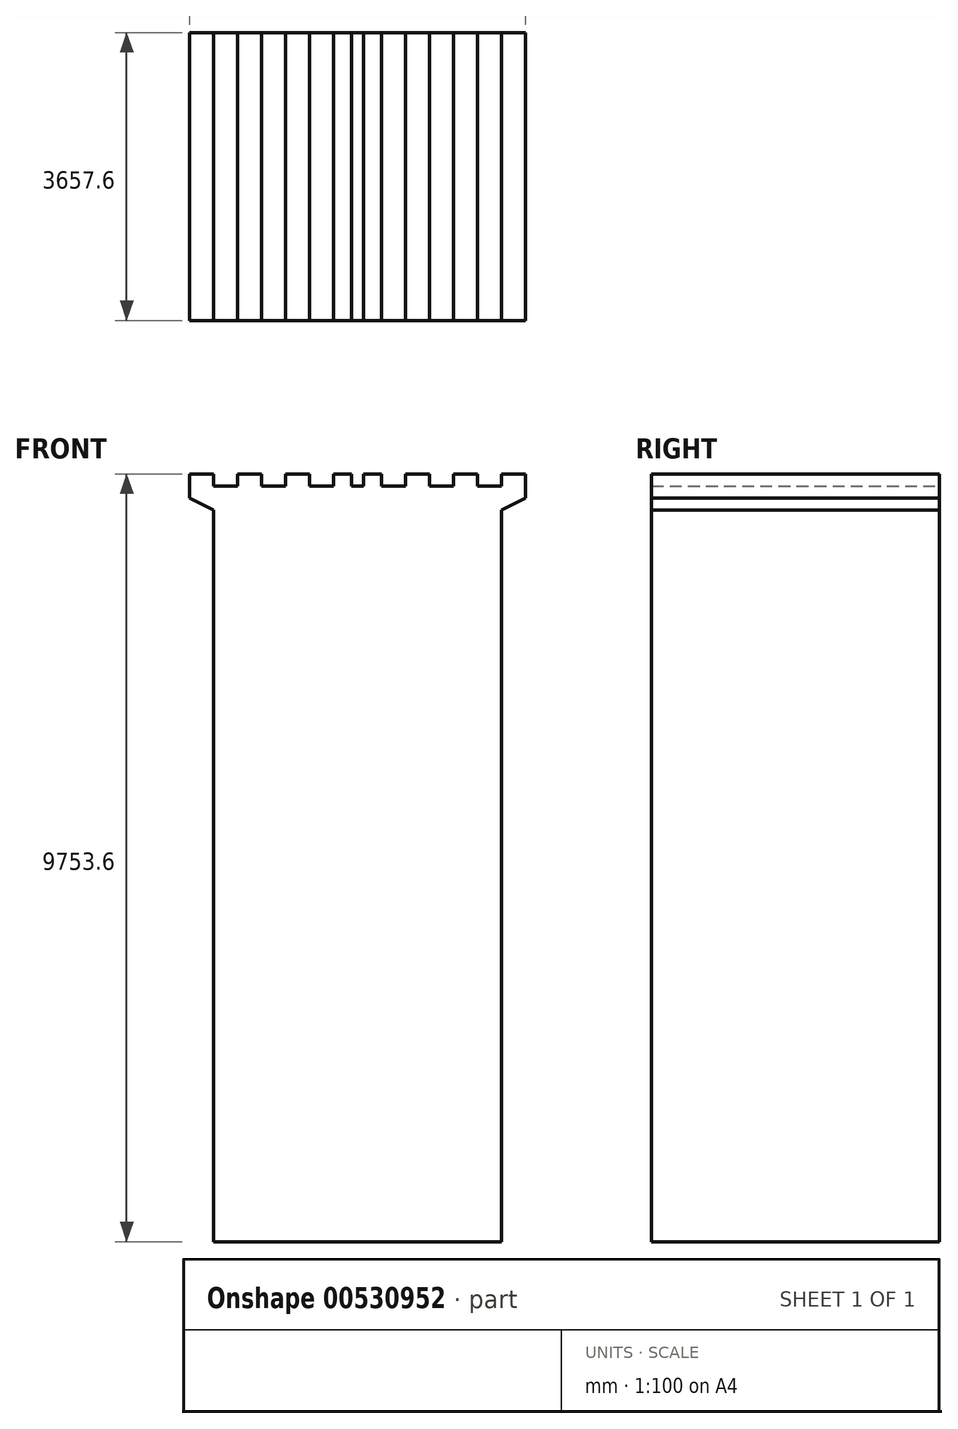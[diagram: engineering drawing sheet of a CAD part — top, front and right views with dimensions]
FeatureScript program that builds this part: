
annotation { "Feature Type Name" : "Feature", "Feature Type Description" : "" }
export const myFeature = defineFeature(function(context is Context, id is Id, definition is map)
    precondition{}
    {
        {
            var Q0;
            Q0=qCreatedBy(makeId("Front.planeOp"),FACE);
            var sketch = newSketch(context, id + "F0", { "sketchPlane" : qUnion([Q0])});
            skLineSegment(sketch, "E0.top", {"start": v(-3041.28, -5600.17) * mm, "end": v(616.32, -5600.17) * mm});
            skLineSegment(sketch, "E0.left", {"start": v(-3041.28, 3696.23) * mm, "end": v(-3041.28, -5600.17) * mm});
            skLineSegment(sketch, "E0.right", {"start": v(616.32, 3696.23) * mm, "end": v(616.32, -5600.17) * mm});
            skPoint(sketch, "E1.firstSnap0", {"position": v(-1212.48, 3848.63) * mm});
            skLineSegment(sketch, "E1.top", {"start": v(921.12, 4153.43) * mm, "end": v(616.32, 4153.43) * mm});
            skLineSegment(sketch, "E1.left", {"start": v(921.12, 3848.63) * mm, "end": v(921.12, 4153.43) * mm});
            skLineSegment(sketch, "E1.right", {"start": v(-3346.08, 3848.63) * mm, "end": v(-3346.08, 4153.43) * mm});
            skLineSegment(sketch, "E2", {"start": v(-3041.28, 4153.43) * mm, "end": v(-3041.28, 4001.03) * mm});
            skLineSegment(sketch, "E3", {"start": v(-3041.28, 4001.03) * mm, "end": v(-2736.48, 4001.03) * mm});
            skLineSegment(sketch, "E4", {"start": v(-2736.48, 4001.03) * mm, "end": v(-2736.48, 4153.43) * mm});
            skLineSegment(sketch, "E5.trimOffspring", {"start": v(-3041.28, 4153.43) * mm, "end": v(-3346.08, 4153.43) * mm});
            skLineSegment(sketch, "E6", {"start": v(-3346.08, 3848.63) * mm, "end": v(-3041.28, 3696.23) * mm});
            skPoint(sketch, "E7.orphan", {"position": v(-3041.28, 3848.63) * mm});
            skLineSegment(sketch, "E8.MirrorCS", {"start": v(-2431.68, 4153.43) * mm, "end": v(-2431.68, 4001.03) * mm});
            skLineSegment(sketch, "E9", {"start": v(-2431.68, 4001.03) * mm, "end": v(-2126.88, 4001.03) * mm});
            skLineSegment(sketch, "E10", {"start": v(-2126.88, 4001.03) * mm, "end": v(-2126.88, 4153.43) * mm});
            skLineSegment(sketch, "E11.trimOffspring", {"start": v(-2431.68, 4153.43) * mm, "end": v(-2736.48, 4153.43) * mm});
            skLineSegment(sketch, "E12", {"start": v(-2584.08, 4153.43) * mm, "end": v(-2584.08, 4001.03) * mm, "construction": true});
            skLineSegment(sketch, "E13", {"start": v(-2279.28, 4001.03) * mm, "end": v(-2279.28, 4153.43) * mm, "construction": true});
            skLineSegment(sketch, "E14.MirrorCS", {"start": v(-2888.88, 4001.03) * mm, "end": v(-2888.88, 4153.43) * mm, "construction": true});
            skLineSegment(sketch, "E15", {"start": v(-2126.88, 4001.03) * mm, "end": v(-1974.48, 4001.03) * mm, "construction": true});
            skLineSegment(sketch, "E16", {"start": v(-1974.48, 4001.03) * mm, "end": v(-1822.08, 4001.03) * mm, "construction": true});
            skLineSegment(sketch, "E17", {"start": v(-1822.08, 4001.03) * mm, "end": v(-1669.68, 4001.03) * mm, "construction": true});
            skLineSegment(sketch, "E18", {"start": v(-1669.68, 4001.03) * mm, "end": v(-1517.28, 4001.03) * mm, "construction": true});
            skLineSegment(sketch, "E19", {"start": v(-1517.28, 4001.03) * mm, "end": v(-1364.88, 4001.03) * mm, "construction": true});
            skLineSegment(sketch, "E20", {"start": v(-1364.88, 4001.03) * mm, "end": v(-1212.48, 4001.03) * mm, "construction": true});
            skLineSegment(sketch, "E21", {"start": v(-1212.48, 4001.03) * mm, "end": v(-1060.08, 4001.03) * mm, "construction": true});
            skLineSegment(sketch, "E22", {"start": v(-1822.08, 4001.03) * mm, "end": v(-1822.08, 4153.43) * mm});
            skLineSegment(sketch, "E23", {"start": v(-1822.08, 4001.03) * mm, "end": v(-1517.28, 4001.03) * mm});
            skLineSegment(sketch, "E24", {"start": v(-1517.28, 4001.03) * mm, "end": v(-1517.28, 4153.43) * mm});
            skLineSegment(sketch, "E25.trimOffspring", {"start": v(-1822.08, 4153.43) * mm, "end": v(-2126.88, 4153.43) * mm});
            skLineSegment(sketch, "E26", {"start": v(-1212.48, 3848.63) * mm, "end": v(-1212.48, -5600.17) * mm, "construction": true});
            skLineSegment(sketch, "E27.MirrorCS", {"start": v(-602.88, 4001.03) * mm, "end": v(-907.68, 4001.03) * mm});
            skLineSegment(sketch, "E28.MirrorCS", {"start": v(-602.88, 4001.03) * mm, "end": v(-755.28, 4001.03) * mm, "construction": true});
            skLineSegment(sketch, "E29.MirrorCS", {"start": v(-602.88, 4001.03) * mm, "end": v(-602.88, 4153.43) * mm});
            skLineSegment(sketch, "E30.MirrorCS", {"start": v(-450.48, 4001.03) * mm, "end": v(-602.88, 4001.03) * mm, "construction": true});
            skLineSegment(sketch, "E31.MirrorCS", {"start": v(-907.68, 4001.03) * mm, "end": v(-907.68, 4153.43) * mm});
            skLineSegment(sketch, "E32.MirrorCS", {"start": v(-755.28, 4001.03) * mm, "end": v(-907.68, 4001.03) * mm, "construction": true});
            skLineSegment(sketch, "E33.MirrorCS", {"start": v(6.72, 4153.43) * mm, "end": v(311.52, 4153.43) * mm});
            skLineSegment(sketch, "E34.MirrorCS", {"start": v(311.52, 4001.03) * mm, "end": v(311.52, 4153.43) * mm});
            skLineSegment(sketch, "E35.MirrorCS", {"start": v(6.72, 4153.43) * mm, "end": v(6.72, 4001.03) * mm});
            skLineSegment(sketch, "E36.MirrorCS", {"start": v(-907.68, 4001.03) * mm, "end": v(-1060.08, 4001.03) * mm, "construction": true});
            skLineSegment(sketch, "E37.MirrorCS", {"start": v(463.92, 4001.03) * mm, "end": v(463.92, 4153.43) * mm, "construction": true});
            skLineSegment(sketch, "E38.MirrorCS", {"start": v(-145.68, 4001.03) * mm, "end": v(-145.68, 4153.43) * mm, "construction": true});
            skLineSegment(sketch, "E39.MirrorCS", {"start": v(616.32, 4153.43) * mm, "end": v(616.32, 4001.03) * mm});
            skLineSegment(sketch, "E40.MirrorCS", {"start": v(-298.08, 4001.03) * mm, "end": v(-298.08, 4153.43) * mm});
            skLineSegment(sketch, "E41.MirrorCS", {"start": v(6.72, 4001.03) * mm, "end": v(-298.08, 4001.03) * mm});
            skLineSegment(sketch, "E42.MirrorCS", {"start": v(-298.08, 4001.03) * mm, "end": v(-450.48, 4001.03) * mm, "construction": true});
            skLineSegment(sketch, "E43.MirrorCS", {"start": v(159.12, 4153.43) * mm, "end": v(159.12, 4001.03) * mm, "construction": true});
            skLineSegment(sketch, "E44.MirrorCS", {"start": v(616.32, 4001.03) * mm, "end": v(311.52, 4001.03) * mm});
            skLineSegment(sketch, "E45.MirrorCS", {"start": v(-1060.08, 4001.03) * mm, "end": v(-1212.48, 4001.03) * mm, "construction": true});
            skLineSegment(sketch, "E46.MirrorCS", {"start": v(-1212.48, 4001.03) * mm, "end": v(-1364.88, 4001.03) * mm, "construction": true});
            skLineSegment(sketch, "E47.MirrorCS", {"start": v(616.32, 4153.43) * mm, "end": v(921.12, 4153.43) * mm});
            skLineSegment(sketch, "E48.MirrorCS", {"start": v(921.12, 3848.63) * mm, "end": v(616.32, 3696.23) * mm});
            skPoint(sketch, "E49.MirrorP", {"position": v(616.32, 3848.63) * mm});
            skLineSegment(sketch, "E50.MirrorCS", {"start": v(616.32, -5600.17) * mm, "end": v(-3041.28, -5600.17) * mm});
            skLineSegment(sketch, "E51.trimOffspring", {"start": v(-907.68, 4153.43) * mm, "end": v(-1136.28, 4153.43) * mm});
            skLineSegment(sketch, "E52.trimOffspring", {"start": v(-298.08, 4153.43) * mm, "end": v(-602.88, 4153.43) * mm});
            skLineSegment(sketch, "E53.trimOffspring", {"start": v(311.52, 4153.43) * mm, "end": v(6.72, 4153.43) * mm});
            skLineSegment(sketch, "E54", {"start": v(-1288.68, 4001.03) * mm, "end": v(-1288.68, 4153.43) * mm});
            skLineSegment(sketch, "E55", {"start": v(-1136.28, 4001.03) * mm, "end": v(-1136.28, 4153.43) * mm});
            skLineSegment(sketch, "E56.trimOffspring", {"start": v(-1288.68, 4153.43) * mm, "end": v(-1517.28, 4153.43) * mm});
            skLineSegment(sketch, "E57", {"start": v(-1288.68, 4001.03) * mm, "end": v(-1136.28, 4001.03) * mm});
            skSolve(sketch);
        }
        {
            var Q0;
            Q0=makeQuery(id+"F0.imprint","IMPRINT",FACE,{"disambiguationData":[TD([[makeQuery(id+"F0.imprint","IMPRINT",EDGE,{"derivedFrom":sQuery(id+"F0.wireOp",EDGE,"E0.left")}),1.0]])]});
            extrude(context, id + "F1", {"entities" : qUnion([Q0]), "depth" : 3657.6 * mm, "offsetDistance" : 30.48 * mm});
        }
    });
